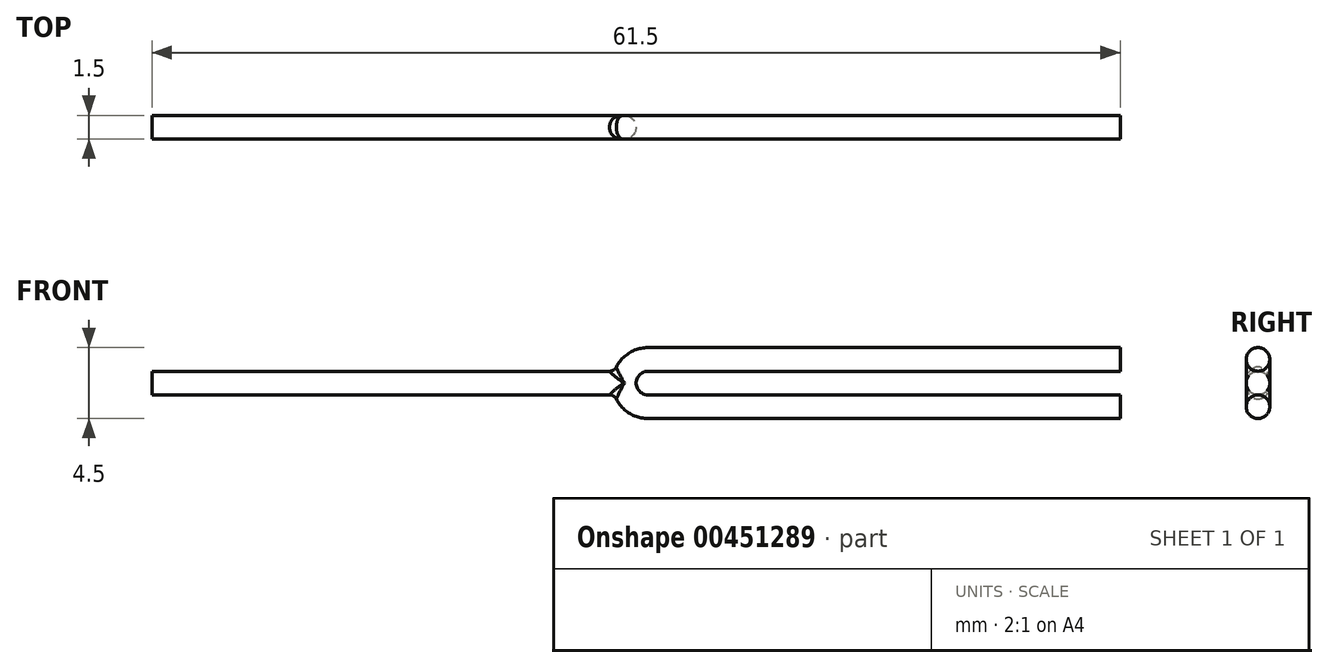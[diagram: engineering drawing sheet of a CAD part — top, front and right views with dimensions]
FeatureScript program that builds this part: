
annotation { "Feature Type Name" : "Feature", "Feature Type Description" : "" }
export const myFeature = defineFeature(function(context is Context, id is Id, definition is map)
    precondition{}
    {
        {
            var Q0;
            Q0=qCreatedBy(makeId("Front.planeOp"),FACE);
            var sketch = newSketch(context, id + "F0", { "sketchPlane" : qUnion([Q0])});
            skLineSegment(sketch, "E0", {"start": v(0, 0) * mm, "end": v(-30, 0) * mm});
            skArc(sketch, "E1", {"start": v(-30, 3) * mm, "mid": v(-31.5, 1.5) * mm, "end": v(-30, 0) * mm});
            skLineSegment(sketch, "E2", {"start": v(-30, 3) * mm, "end": v(0, 3) * mm});
            skLineSegment(sketch, "E3", {"start": v(-31.5, 1.5) * mm, "end": v(-61.5, 1.5) * mm});
            skSolve(sketch);
        }
        {
            var Q0;
            Q0=qCreatedBy(makeId("Right.planeOp"),FACE);
            var sketch = newSketch(context, id + "F1", { "sketchPlane" : qUnion([Q0])});
            skCircle(sketch, "E4", {"center": v(0, 0) * mm, "radius": 0.75 * mm});
            skSolve(sketch);
        }
        {
            var Q0;
            Q0 = qSketchRegion(id + "F1", true);
            var Q1;
            Q1=sQuery(id+"F0.wireOp",EDGE,"E0");
            var Q2;
            Q2=sQuery(id+"F0.wireOp",EDGE,"E1");
            var Q3;
            Q3=sQuery(id+"F0.wireOp",EDGE,"E2");
            sweep(context, id + "F2", {"profiles" : qUnion([Q0]), "path" : qUnion([Q1, Q2, Q3])});
        }
        {
            var Q0;
            Q0=qCreatedBy(makeId("Right.planeOp"),FACE);
            var Q1;
            Q1=sQuery(id+"F0.wireOp",VERTEX,"E3.end");
            cPlane(context, id + "F3", {"entities" : qUnion([Q0, Q1]), "cplaneType" : CPlaneType.PLANE_POINT, "offset" : 100 * mm, "oppositeDirection" : true, "width" : 150 * mm, "height" : 150 * mm});
        }
        {
            var Q0;
            Q0=qCreatedBy(id+"F3.planeOp",FACE);
            var sketch = newSketch(context, id + "F4", { "sketchPlane" : qUnion([Q0])});
            skCircle(sketch, "E5", {"center": v(0, 1.5) * mm, "radius": 0.75 * mm});
            skSolve(sketch);
        }
        {
            var Q0;
            Q0 = qSketchRegion(id + "F4", true);
            var Q1;
            Q1=sQuery(id+"F0.wireOp",EDGE,"E3");
            sweep(context, id + "F5", {"operationType" : NewBodyOperationType.ADD, "profiles" : qUnion([Q0]), "path" : qUnion([Q1])});
        }
        {
            var Q0;
            Q0=makeQuery(id+"F5.boolean.opBoolean","INTERSECT",EDGE,{"disambiguationData":[OD(0.0)],"derivedFrom":[makeQuery(id+"F2.opSweep","SWEPT_FACE",FACE,{"disambiguationData":[OSD([sQuery(id+"F0.wireOp",EDGE,"E1"),sQuery(id+"F1.wireOp",EDGE,"E4")])]}),makeQuery(id+"F5.opSweep","SWEPT_FACE",FACE,{"disambiguationData":[OSD([sQuery(id+"F0.wireOp",EDGE,"E3"),sQuery(id+"F4.wireOp",EDGE,"E5")])]})]});
            var Q1;
            Q1=makeQuery(id+"F5.boolean.opBoolean","INTERSECT",EDGE,{"disambiguationData":[OD(1.0)],"derivedFrom":[makeQuery(id+"F2.opSweep","SWEPT_FACE",FACE,{"disambiguationData":[OSD([sQuery(id+"F0.wireOp",EDGE,"E1"),sQuery(id+"F1.wireOp",EDGE,"E4")])]}),makeQuery(id+"F5.opSweep","SWEPT_FACE",FACE,{"disambiguationData":[OSD([sQuery(id+"F0.wireOp",EDGE,"E3"),sQuery(id+"F4.wireOp",EDGE,"E5")])]})]});
            fillet(context, id + "F6", {"entities" : qUnion([Q0, Q1]), "radius" : 0.5 * mm, "tangentPropagation" : true, "allowEdgeOverflow" : false});
        }
    });
